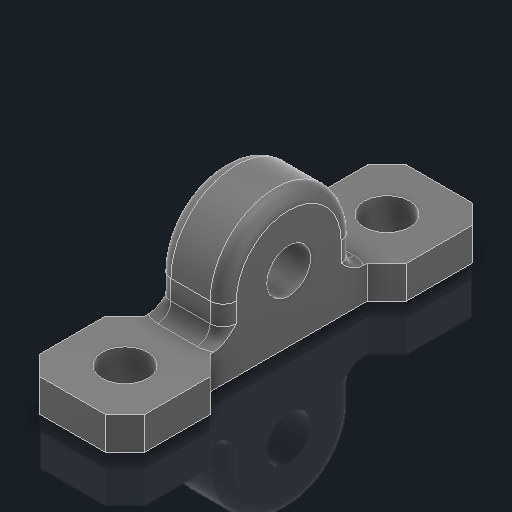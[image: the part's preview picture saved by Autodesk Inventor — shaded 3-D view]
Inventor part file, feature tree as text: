
AUTODESK INVENTOR PART (.ipt)
format: ipt  version: 2023.2 (Build 272271030, 271C)  size: 224,256 bytes
history: native  units: in
note: dims shown in document units (in); Inventor stores cm internally (conversion verified against a paired STEP export)
features: other x3, sketch x3
ambient origin geometry x8: Origin, YZ Plane, XZ Plane, XY Plane, X Axis, Y Axis, Z Axis, Center Point
bodies: Solid1 (feature_tree)
feature tree (6):
  other  "LS Pillow Bearing Block.ipt"
  other  "Solid1::LS Pillow Bearing Block.ipt"
  other  "TaggingFeature1"
  sketch  "Sketch1"  dims[d0=0.3937in]
  sketch  "Sketch2"
  sketch  "Sketch3"
